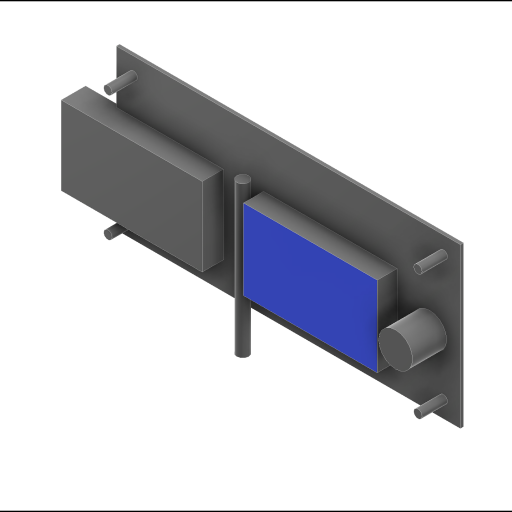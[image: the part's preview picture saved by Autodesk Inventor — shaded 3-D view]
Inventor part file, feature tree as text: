
AUTODESK INVENTOR PART (.ipt)
format: ipt  version: 2023 (Build 270158000, 158)  size: 192,512 bytes
history: native  units: in
note: dims shown in document units (in); Inventor stores cm internally (conversion verified against a paired STEP export)
features: extrude x6, sketch x6
ambient origin geometry x8: Origin, YZ Plane, XZ Plane, XY Plane, X Axis, Y Axis, Z Axis, Center Point
bodies: Solid1 (feature_tree)
feature tree (12):
  extrude  "Extrusion1"  Depth=4.6875in
  extrude  "Clearance Distance"  Depth=0.25in
  extrude  "Extrusion3"  Depth=0.25in
  extrude  "Extrusion4"  Depth=0.5in
  extrude  "Extrusion5"  Depth=0.5in
  extrude  "Extrusion6"  Depth=0.5in
  sketch  "Sketch1"  dims[d0=10.125in d1=4.6875in]
  sketch  "Sketch2"  dims[d2=0.0938in d3=0.0in d4=0.25in]
  sketch  "Sketch3"  dims[d5=0.25in d6=0.25in]
  sketch  "Sketch4"  dims[d7=0.25in d8=0.5in]
  sketch  "Sketch6"  dims[d9=0.5in d10=0.5in]
  sketch  "Sketch7"  dims[d11=0.5in d12=0.5in d13=0.5in d14=0.5in d15=0.5in d16=0.75in d17=0.0in d18=0.7188in d19=1.5625in d20=3.875in d21=1.0in d22=0.0in d23=3.1496in d24=0.0in d25=1.0in d26=2.625in d27=0.9063in d28=1.0in d29=0.0in d30=4.0in d31=1.0in d32=3.4375in d33=0.0in d34=0.0in d35=4.3307in d36=8.2677in d37=0.7874in d38=3.1496in d39=0.5906in d40=0.0in]
